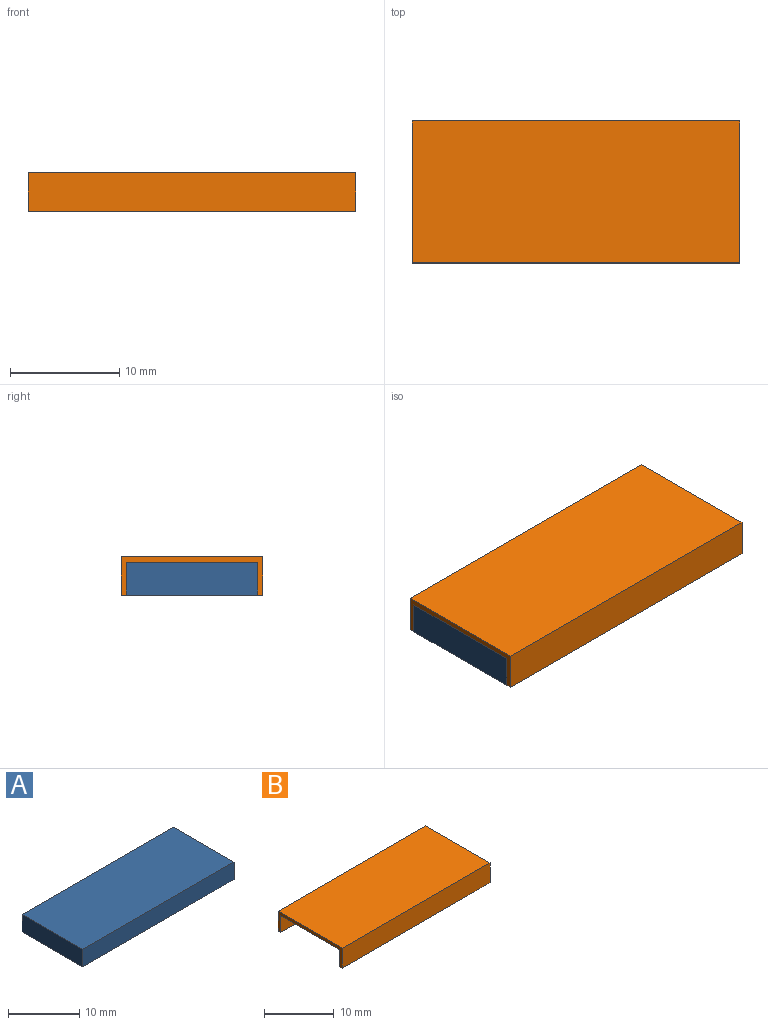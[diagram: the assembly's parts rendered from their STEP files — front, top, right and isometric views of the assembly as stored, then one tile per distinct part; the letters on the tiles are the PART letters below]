
ASSEMBLY  parts=2 mates=1
PART A: 6 faces, bbox 30x12x3 mm
  f0: plane 12x3mm, normal (1,0,0), area 36mm2, adj f1,f3,f4,f5
  f1: plane 30x3mm, normal (0,1,0), area 90mm2, adj f0,f2,f4,f5
  f2: plane 12x3mm, normal (-1,0,0), area 36mm2, adj f1,f3,f4,f5
  f3: plane 30x3mm, normal (0,-1,0), area 90mm2, adj f0,f2,f4,f5
  f4: plane 30x12mm, normal (0,0,1), area 360mm2, adj f0,f1,f2,f3
  f5: plane 30x12mm, normal (0,0,-1), area 360mm2, adj f0,f1,f2,f3
PART B: 10 faces, bbox 30x13x3.5 mm
  f0: plane 30x3mm, normal (0,-1,0), area 90mm2, adj f1,f7,f8,f9
  f1: plane 30x0.5mm, normal (0,0,-1), area 15mm2, adj f0,f2,f8,f9
  f2: plane 30x3.5mm, normal (0,1,0), area 105mm2, adj f1,f3,f8,f9
  f3: plane 30x13mm, normal (0,0,1), area 390mm2, adj f2,f4,f8,f9
  f4: plane 30x3.5mm, normal (0,-1,0), area 105mm2, adj f3,f5,f8,f9
  f5: plane 30x0.5mm, normal (0,0,-1), area 15mm2, adj f4,f6,f8,f9
  f6: plane 30x3mm, normal (0,1,0), area 90mm2, adj f5,f7,f8,f9
  f7: plane 30x12mm, normal (0,0,-1), area 360mm2, adj f0,f6,f8,f9
  f8: plane 13x3.5mm, normal (1,0,0), area 9.5mm2, adj f0,f1,f2,f3,f4,f5,f6,f7
  f9: plane 13x3.5mm, normal (-1,0,0), area 9.5mm2, adj f0,f1,f2,f3,f4,f5,f6,f7
PLACE A t=(35.21,22.9,6.15)mm
PLACE B t=(20.21,22.14,6.15)mm
MATE fastened A.f4 <-> B.f7  axis (0,0,1) through (35.21,22.9,9.15)mm
